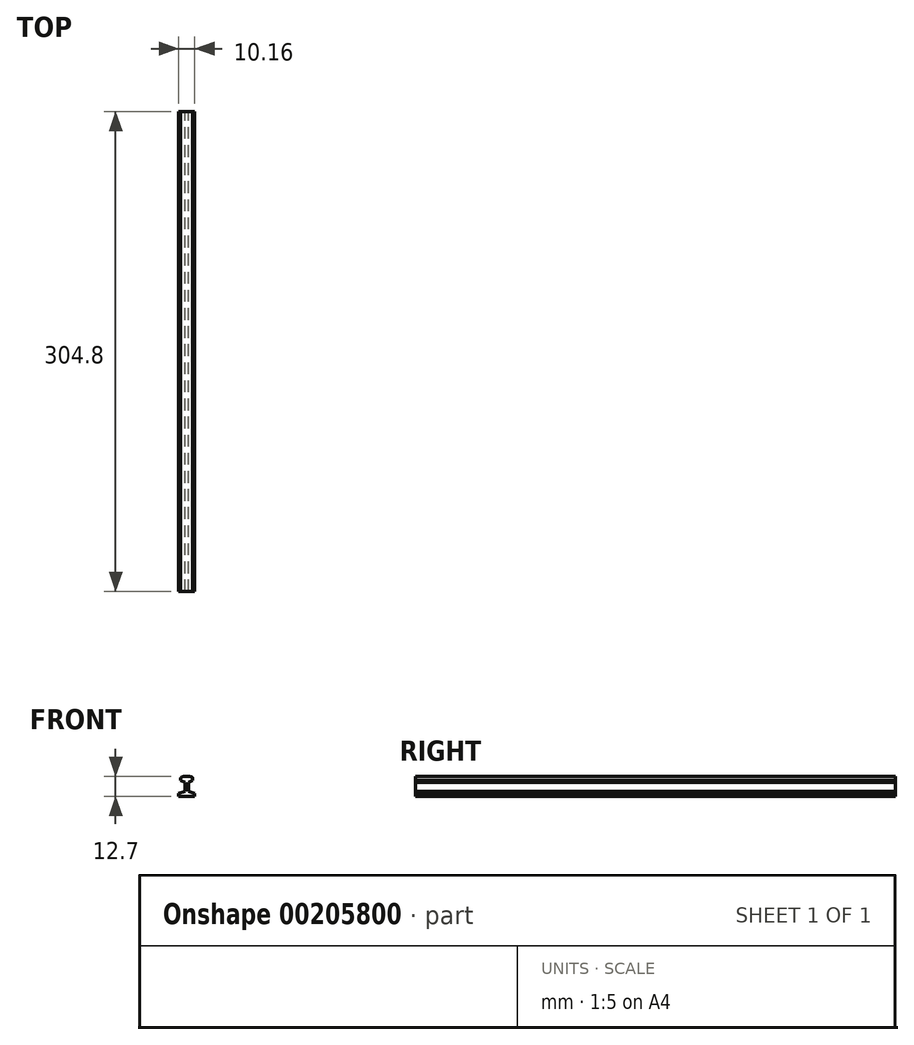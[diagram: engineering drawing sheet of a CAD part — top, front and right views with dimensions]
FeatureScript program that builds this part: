
annotation { "Feature Type Name" : "Feature", "Feature Type Description" : "" }
export const myFeature = defineFeature(function(context is Context, id is Id, definition is map)
    precondition{}
    {
        {
            var Q0;
            Q0=qCreatedBy(makeId("Front.planeOp"),FACE);
            var sketch = newSketch(context, id + "F0", { "sketchPlane" : qUnion([Q0])});
            skLineSegment(sketch, "E0", {"start": v(0, 0) * mm, "end": v(-5.08, 0) * mm});
            skLineSegment(sketch, "E1", {"start": v(-5.08, 0) * mm, "end": v(-5.08, 1.9) * mm});
            skLineSegment(sketch, "E2", {"start": v(-5.08, 1.9) * mm, "end": v(-1.02, 3.18) * mm});
            skLineSegment(sketch, "E3", {"start": v(-1.02, 3.18) * mm, "end": v(-1.02, 8.9) * mm});
            skLineSegment(sketch, "E4", {"start": v(-1.02, 8.9) * mm, "end": v(-3.81, 10.16) * mm});
            skLineSegment(sketch, "E5", {"start": v(-3.81, 10.16) * mm, "end": v(-3.81, 11.43) * mm});
            skLineSegment(sketch, "E6", {"start": v(0, 12.7) * mm, "end": v(0, 0) * mm, "construction": true});
            skArc(sketch, "E7", {"start": v(0, 12.7) * mm, "mid": v(-1.5, 12.63) * mm, "end": v(-2.98, 12.43) * mm});
            skArc(sketch, "E8", {"start": v(-2.98, 12.43) * mm, "mid": v(-3.57, 12.08) * mm, "end": v(-3.81, 11.43) * mm});
            skLineSegment(sketch, "E9", {"start": v(0, 12.7) * mm, "end": v(2.98, 12.7) * mm, "construction": true});
            skLineSegment(sketch, "E10.MirrorCS", {"start": v(0, 0) * mm, "end": v(5.08, 0) * mm});
            skLineSegment(sketch, "E11.MirrorCS", {"start": v(1.02, 3.18) * mm, "end": v(1.02, 8.9) * mm});
            skLineSegment(sketch, "E12.MirrorCS", {"start": v(1.02, 8.9) * mm, "end": v(3.81, 10.16) * mm});
            skLineSegment(sketch, "E13.MirrorCS", {"start": v(5.08, 1.9) * mm, "end": v(1.02, 3.18) * mm});
            skLineSegment(sketch, "E14.MirrorCS", {"start": v(3.81, 10.16) * mm, "end": v(3.81, 11.43) * mm});
            skLineSegment(sketch, "E15.MirrorCS", {"start": v(5.08, 0) * mm, "end": v(5.08, 1.9) * mm});
            skArc(sketch, "E16.MirrorCS", {"start": v(2.98, 12.43) * mm, "mid": v(3.57, 12.08) * mm, "end": v(3.81, 11.43) * mm});
            skArc(sketch, "E17.MirrorCS", {"start": v(0, 12.7) * mm, "mid": v(1.5, 12.63) * mm, "end": v(2.98, 12.43) * mm});
            skSolve(sketch);
        }
        {
            var Q0;
            Q0 = qSketchRegion(id + "F0", true);
            extrude(context, id + "F1", {"entities" : qUnion([Q0]), "depth" : 304.8 * mm});
        }
    });
